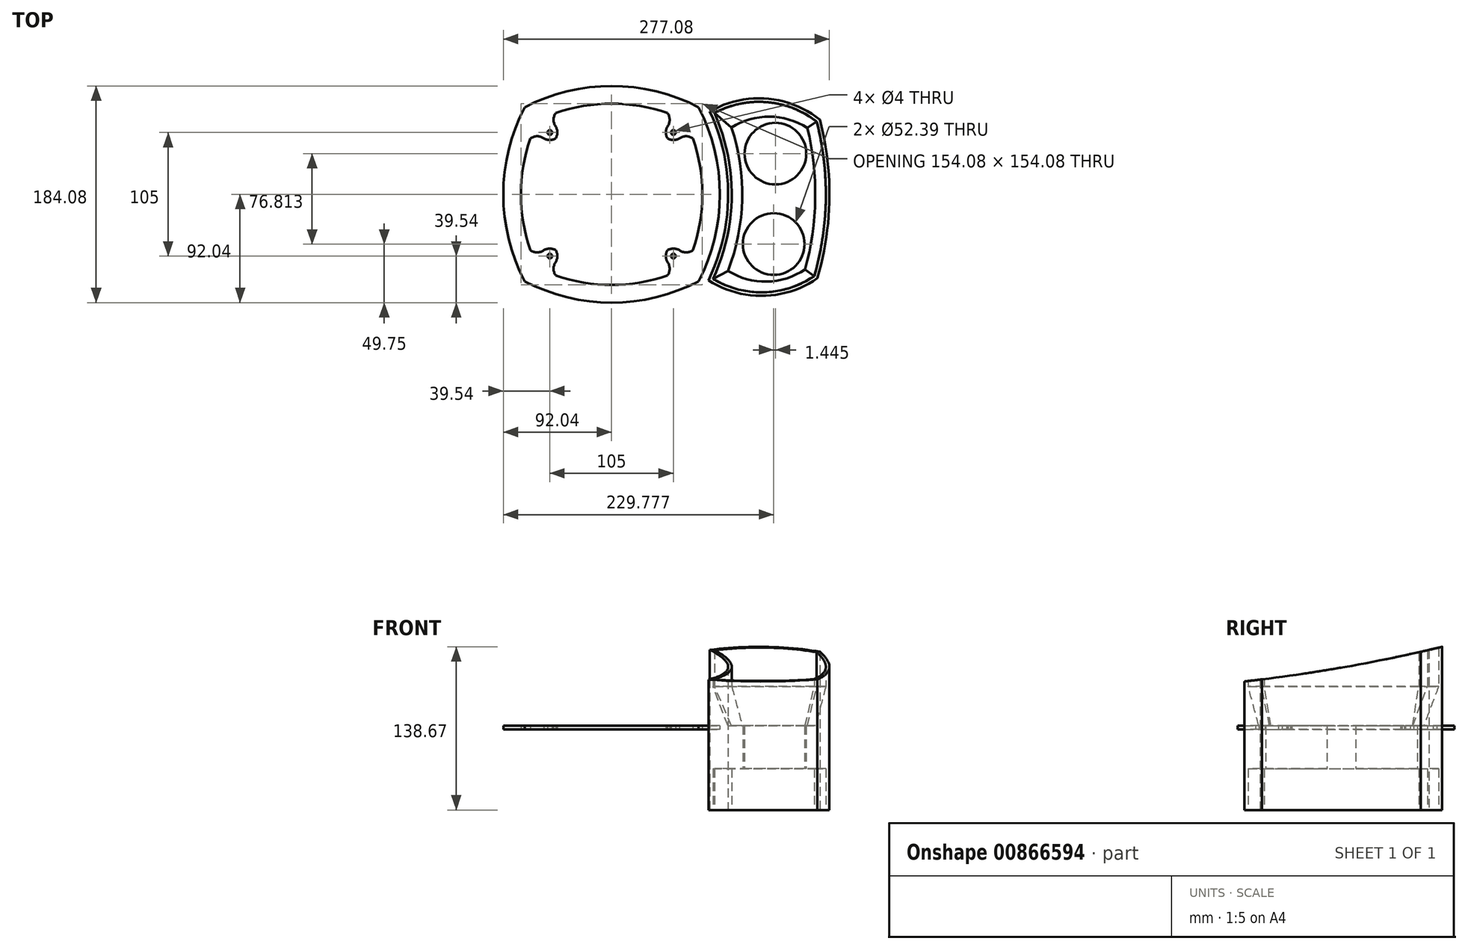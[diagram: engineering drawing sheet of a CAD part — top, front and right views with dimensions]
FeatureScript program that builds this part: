
annotation { "Feature Type Name" : "Feature", "Feature Type Description" : "" }
export const myFeature = defineFeature(function(context is Context, id is Id, definition is map)
    precondition{}
    {
        {
            var Q0;
            Q0=qCreatedBy(makeId("Top.planeOp"),FACE);
            var sketch = newSketch(context, id + "F0", { "sketchPlane" : qUnion([Q0])});
            skLineSegment(sketch, "E0.bottom", {"start": v(59, 59) * mm, "end": v(-59, 59) * mm, "construction": true});
            skLineSegment(sketch, "E0.top", {"start": v(59, -59) * mm, "end": v(-59, -59) * mm, "construction": true});
            skLineSegment(sketch, "E0.left", {"start": v(59, 59) * mm, "end": v(59, -59) * mm, "construction": true});
            skLineSegment(sketch, "E0.right", {"start": v(-59, 59) * mm, "end": v(-59, -59) * mm, "construction": true});
            skPoint(sketch, "E0.middle", {"position": v(0, 0) * mm});
            skArc(sketch, "E1", {"start": v(59, 59) * mm, "mid": v(0, 72.04) * mm, "end": v(-59, 59) * mm, "construction": true});
            skArc(sketch, "E2", {"start": v(59, -59) * mm, "mid": v(72.04, 0) * mm, "end": v(59, 59) * mm, "construction": true});
            skArc(sketch, "E3", {"start": v(-59, -59) * mm, "mid": v(0, -72.04) * mm, "end": v(59, -59) * mm, "construction": true});
            skArc(sketch, "E4", {"start": v(-59, 59) * mm, "mid": v(-72.04, 0) * mm, "end": v(-59, -59) * mm, "construction": true});
            skArc(sketch, "E5.0", {"start": v(62.76, 62.76) * mm, "mid": v(0, 77.04) * mm, "end": v(-62.76, 62.76) * mm});
            skArc(sketch, "E5.1", {"start": v(62.76, -62.76) * mm, "mid": v(77.04, 0) * mm, "end": v(62.76, 62.76) * mm});
            skArc(sketch, "E5.2", {"start": v(-62.76, -62.76) * mm, "mid": v(0, -77.04) * mm, "end": v(62.76, -62.76) * mm});
            skArc(sketch, "E5.3", {"start": v(-62.76, 62.76) * mm, "mid": v(-77.04, 0) * mm, "end": v(-62.76, -62.76) * mm});
            skArc(sketch, "E6.0", {"start": v(73.93, 73.93) * mm, "mid": v(0, 92.04) * mm, "end": v(-73.93, 73.93) * mm});
            skArc(sketch, "E6.1", {"start": v(73.93, -73.93) * mm, "mid": v(92.04, 0) * mm, "end": v(73.93, 73.93) * mm});
            skArc(sketch, "E6.2", {"start": v(-73.93, -73.93) * mm, "mid": v(0, -92.04) * mm, "end": v(73.93, -73.93) * mm});
            skArc(sketch, "E6.3", {"start": v(-73.93, 73.93) * mm, "mid": v(-92.04, 0) * mm, "end": v(-73.93, -73.93) * mm});
            skLineSegment(sketch, "E7.bottom", {"start": v(52.5, 52.5) * mm, "end": v(-52.5, 52.5) * mm, "construction": true});
            skLineSegment(sketch, "E7.top", {"start": v(52.5, -52.5) * mm, "end": v(-52.5, -52.5) * mm, "construction": true});
            skLineSegment(sketch, "E7.left", {"start": v(52.5, 52.5) * mm, "end": v(52.5, -52.5) * mm, "construction": true});
            skLineSegment(sketch, "E7.right", {"start": v(-52.5, 52.5) * mm, "end": v(-52.5, -52.5) * mm, "construction": true});
            skCircle(sketch, "E8", {"center": v(-52.5, 52.5) * mm, "radius": 2 * mm});
            skCircle(sketch, "E9", {"center": v(52.5, 52.5) * mm, "radius": 2 * mm});
            skCircle(sketch, "E10", {"center": v(52.5, -52.5) * mm, "radius": 2 * mm});
            skCircle(sketch, "E11", {"center": v(-52.5, -52.5) * mm, "radius": 2 * mm});
            skLineSegment(sketch, "E12.bottom", {"start": v(-47.5, 57.5) * mm, "end": v(-57.5, 57.5) * mm, "construction": true});
            skLineSegment(sketch, "E12.top", {"start": v(-47.5, 47.5) * mm, "end": v(-57.5, 47.5) * mm, "construction": true});
            skLineSegment(sketch, "E12.left", {"start": v(-47.5, 57.5) * mm, "end": v(-47.5, 47.5) * mm, "construction": true});
            skLineSegment(sketch, "E12.right", {"start": v(-57.5, 57.5) * mm, "end": v(-57.5, 47.5) * mm, "construction": true});
            skLineSegment(sketch, "E13.bottom", {"start": v(47.5, 57.5) * mm, "end": v(57.5, 57.5) * mm, "construction": true});
            skLineSegment(sketch, "E13.top", {"start": v(47.5, 47.5) * mm, "end": v(57.5, 47.5) * mm, "construction": true});
            skLineSegment(sketch, "E13.left", {"start": v(47.5, 57.5) * mm, "end": v(47.5, 47.5) * mm, "construction": true});
            skLineSegment(sketch, "E13.right", {"start": v(57.5, 57.5) * mm, "end": v(57.5, 47.5) * mm, "construction": true});
            skLineSegment(sketch, "E14.bottom", {"start": v(57.5, -47.5) * mm, "end": v(47.5, -47.5) * mm, "construction": true});
            skLineSegment(sketch, "E14.top", {"start": v(57.5, -57.5) * mm, "end": v(47.5, -57.5) * mm, "construction": true});
            skLineSegment(sketch, "E14.left", {"start": v(57.5, -47.5) * mm, "end": v(57.5, -57.5) * mm, "construction": true});
            skLineSegment(sketch, "E14.right", {"start": v(47.5, -47.5) * mm, "end": v(47.5, -57.5) * mm, "construction": true});
            skLineSegment(sketch, "E15.bottom", {"start": v(-47.5, -47.5) * mm, "end": v(-57.5, -47.5) * mm, "construction": true});
            skLineSegment(sketch, "E15.top", {"start": v(-47.5, -57.5) * mm, "end": v(-57.5, -57.5) * mm, "construction": true});
            skLineSegment(sketch, "E15.left", {"start": v(-47.5, -47.5) * mm, "end": v(-47.5, -57.5) * mm, "construction": true});
            skLineSegment(sketch, "E15.right", {"start": v(-57.5, -47.5) * mm, "end": v(-57.5, -57.5) * mm, "construction": true});
            skArc(sketch, "E16", {"start": v(-47.5, 57.5) * mm, "mid": v(-52.5, 58.84) * mm, "end": v(-57.5, 57.5) * mm});
            skArc(sketch, "E17", {"start": v(-47.5, 47.5) * mm, "mid": v(-46.16, 52.5) * mm, "end": v(-47.5, 57.5) * mm});
            skArc(sketch, "E18", {"start": v(-57.5, 47.5) * mm, "mid": v(-52.5, 46.16) * mm, "end": v(-47.5, 47.5) * mm});
            skArc(sketch, "E19", {"start": v(-57.5, 57.5) * mm, "mid": v(-58.84, 52.5) * mm, "end": v(-57.5, 47.5) * mm});
            skArc(sketch, "E20", {"start": v(-47.5, 69.04) * mm, "mid": v(-49.33, 63.27) * mm, "end": v(-47.5, 57.5) * mm});
            skArc(sketch, "E21", {"start": v(-57.5, 47.5) * mm, "mid": v(-63.27, 49.33) * mm, "end": v(-69.04, 47.5) * mm});
            skArc(sketch, "E22", {"start": v(47.5, 47.5) * mm, "mid": v(52.5, 46.16) * mm, "end": v(57.5, 47.5) * mm});
            skArc(sketch, "E23", {"start": v(47.5, 57.5) * mm, "mid": v(46.16, 52.5) * mm, "end": v(47.5, 47.5) * mm});
            skArc(sketch, "E24", {"start": v(57.5, 57.5) * mm, "mid": v(52.5, 58.84) * mm, "end": v(47.5, 57.5) * mm});
            skArc(sketch, "E25", {"start": v(57.5, 47.5) * mm, "mid": v(58.84, 52.5) * mm, "end": v(57.5, 57.5) * mm});
            skArc(sketch, "E26", {"start": v(47.5, 57.5) * mm, "mid": v(49.33, 63.27) * mm, "end": v(47.5, 69.04) * mm});
            skArc(sketch, "E27", {"start": v(69.04, 47.5) * mm, "mid": v(63.27, 49.33) * mm, "end": v(57.5, 47.5) * mm});
            skArc(sketch, "E28", {"start": v(57.5, -47.5) * mm, "mid": v(52.5, -46.16) * mm, "end": v(47.5, -47.5) * mm});
            skArc(sketch, "E29", {"start": v(47.5, -47.5) * mm, "mid": v(46.16, -52.5) * mm, "end": v(47.5, -57.5) * mm});
            skArc(sketch, "E30", {"start": v(47.5, -57.5) * mm, "mid": v(52.5, -58.84) * mm, "end": v(57.5, -57.5) * mm});
            skArc(sketch, "E31", {"start": v(57.5, -57.5) * mm, "mid": v(58.84, -52.5) * mm, "end": v(57.5, -47.5) * mm});
            skArc(sketch, "E32", {"start": v(57.5, -47.5) * mm, "mid": v(63.27, -49.33) * mm, "end": v(69.04, -47.5) * mm});
            skArc(sketch, "E33", {"start": v(47.5, -69.04) * mm, "mid": v(49.33, -63.27) * mm, "end": v(47.5, -57.5) * mm});
            skArc(sketch, "E34", {"start": v(-47.5, -47.5) * mm, "mid": v(-52.5, -46.16) * mm, "end": v(-57.5, -47.5) * mm});
            skArc(sketch, "E35", {"start": v(-47.5, -57.5) * mm, "mid": v(-46.16, -52.5) * mm, "end": v(-47.5, -47.5) * mm});
            skArc(sketch, "E36", {"start": v(-57.5, -57.5) * mm, "mid": v(-52.5, -58.84) * mm, "end": v(-47.5, -57.5) * mm});
            skArc(sketch, "E37", {"start": v(-57.5, -47.5) * mm, "mid": v(-58.84, -52.5) * mm, "end": v(-57.5, -57.5) * mm});
            skArc(sketch, "E38", {"start": v(-69.04, -47.5) * mm, "mid": v(-63.27, -49.33) * mm, "end": v(-57.5, -47.5) * mm});
            skArc(sketch, "E39", {"start": v(-47.5, -57.5) * mm, "mid": v(-49.33, -63.27) * mm, "end": v(-47.5, -69.04) * mm});
            skSolve(sketch);
        }
        {
            var Q0;
            Q0=makeQuery(id+"F0.imprint","IMPRINT",FACE,{"disambiguationData":[TD([[makeQuery(id+"F0.imprint","IMPRINT",EDGE,{"derivedFrom":sQuery(id+"F0.wireOp",EDGE,"E6.0")}),1.0]])]});
            var Q1;
            Q1=makeQuery(id+"F0.imprint","IMPRINT",FACE,{"disambiguationData":[TD([[makeQuery(id+"F0.imprint","IMPRINT",EDGE,{"derivedFrom":sQuery(id+"F0.wireOp",EDGE,"E16")}),-1.0]])]});
            var Q2;
            Q2=makeQuery(id+"F0.imprint","IMPRINT",FACE,{"disambiguationData":[TD([[makeQuery(id+"F0.imprint","IMPRINT",EDGE,{"derivedFrom":sQuery(id+"F0.wireOp",EDGE,"E8")}),-1.0]])]});
            var Q3;
            Q3=makeQuery(id+"F0.imprint","IMPRINT",FACE,{"disambiguationData":[TD([[makeQuery(id+"F0.imprint","IMPRINT",EDGE,{"derivedFrom":sQuery(id+"F0.wireOp",EDGE,"E24")}),-1.0]])]});
            var Q4;
            Q4=makeQuery(id+"F0.imprint","IMPRINT",FACE,{"disambiguationData":[TD([[makeQuery(id+"F0.imprint","IMPRINT",EDGE,{"derivedFrom":sQuery(id+"F0.wireOp",EDGE,"E9")}),-1.0]])]});
            var Q5;
            Q5=makeQuery(id+"F0.imprint","IMPRINT",FACE,{"disambiguationData":[TD([[makeQuery(id+"F0.imprint","IMPRINT",EDGE,{"derivedFrom":sQuery(id+"F0.wireOp",EDGE,"E30")}),-1.0]])]});
            var Q6;
            Q6=makeQuery(id+"F0.imprint","IMPRINT",FACE,{"disambiguationData":[TD([[makeQuery(id+"F0.imprint","IMPRINT",EDGE,{"derivedFrom":sQuery(id+"F0.wireOp",EDGE,"E10")}),-1.0]])]});
            var Q7;
            Q7=makeQuery(id+"F0.imprint","IMPRINT",FACE,{"disambiguationData":[TD([[makeQuery(id+"F0.imprint","IMPRINT",EDGE,{"derivedFrom":sQuery(id+"F0.wireOp",EDGE,"E36")}),-1.0]])]});
            var Q8;
            Q8=makeQuery(id+"F0.imprint","IMPRINT",FACE,{"disambiguationData":[TD([[makeQuery(id+"F0.imprint","IMPRINT",EDGE,{"derivedFrom":sQuery(id+"F0.wireOp",EDGE,"E11")}),-1.0]])]});
            extrude(context, id + "F1", {"entities" : qUnion([Q0, Q1, Q2, Q3, Q4, Q5, Q6, Q7, Q8]), "endBound" : BoundingType.SYMMETRIC, "depth" : 3 * mm, "offsetDistance" : 25 * mm});
        }
        {
            var Q0;
            Q0=qCreatedBy(makeId("Top.planeOp"),FACE);
            var sketch = newSketch(context, id + "F2", { "sketchPlane" : qUnion([Q0])});
            skCircle(sketch, "E40", {"center": v(139.18, 34.52) * mm, "radius": 26.2 * mm});
            skCircle(sketch, "E41.0", {"center": v(139.18, 34.52) * mm, "radius": 31.2 * mm});
            skCircle(sketch, "E42", {"center": v(137.74, -42.3) * mm, "radius": 26.2 * mm});
            skCircle(sketch, "E43.0", {"center": v(137.74, -42.3) * mm, "radius": 31.2 * mm});
            skArc(sketch, "E44.0", {"start": v(118.28, -97.04) * mm, "mid": v(142.04, 0) * mm, "end": v(118.28, 97.04) * mm, "construction": true});
            skArc(sketch, "E45.0", {"start": v(86.1, -71.87) * mm, "mid": v(102.03, -1.53) * mm, "end": v(87.37, 69.09) * mm});
            skArc(sketch, "E46.0", {"start": v(172.19, -69.5) * mm, "mid": v(182, -4.02) * mm, "end": v(174.3, 61.74) * mm});
            skArc(sketch, "E47", {"start": v(174.3, 61.74) * mm, "mid": v(131.92, 78.3) * mm, "end": v(87.37, 69.09) * mm});
            skArc(sketch, "E48", {"start": v(86.1, -71.87) * mm, "mid": v(129.5, -83.25) * mm, "end": v(172.19, -69.5) * mm});
            skArc(sketch, "E49.0", {"start": v(176.95, 63.47) * mm, "mid": v(131.29, 81.36) * mm, "end": v(83.5, 70.36) * mm});
            skArc(sketch, "E49.1", {"start": v(174.77, -71.36) * mm, "mid": v(185, -4.1) * mm, "end": v(176.95, 63.47) * mm});
            skArc(sketch, "E49.2", {"start": v(82.24, -73) * mm, "mid": v(128.75, -86.27) * mm, "end": v(174.77, -71.36) * mm});
            skArc(sketch, "E49.3", {"start": v(82.24, -73) * mm, "mid": v(99.03, -1.46) * mm, "end": v(83.5, 70.36) * mm});
            skSolve(sketch);
        }
        {
            var Q0;
            Q0=makeQuery(id+"F2.imprint","IMPRINT",FACE,{"disambiguationData":[TD([[makeQuery(id+"F2.imprint","IMPRINT",EDGE,{"derivedFrom":sQuery(id+"F2.wireOp",EDGE,"E45.0")}),1.0]])]});
            extrude(context, id + "F3", {"entities" : qUnion([Q0]), "endBound" : BoundingType.SYMMETRIC, "depth" : 140 * mm, "offsetDistance" : 25 * mm});
        }
        {
            var Q0;
            Q0=qCreatedBy(makeId("Right.planeOp"),FACE);
            var sketch = newSketch(context, id + "F4", { "sketchPlane" : qUnion([Q0])});
            skLineSegment(sketch, "E50", {"start": v(0, 0) * mm, "end": v(-487.6, 0) * mm, "construction": true});
            skCircle(sketch, "E51", {"center": v(-240, 1410) * mm, "radius": 1379.34 * mm});
            skCircle(sketch, "E52.MirrorC", {"center": v(-240, -1410) * mm, "radius": 1379.34 * mm});
            skSolve(sketch);
        }
        {
            var Q0;
            Q0=makeQuery(id+"F4.imprint","IMPRINT",FACE,{"disambiguationData":[TD([[makeQuery(id+"F4.imprint","IMPRINT",EDGE,{"derivedFrom":sQuery(id+"F4.wireOp",EDGE,"E51")}),1.0]])]});
            var Q1;
            Q1=makeQuery(id+"F4.imprint","IMPRINT",FACE,{"disambiguationData":[TD([[makeQuery(id+"F4.imprint","IMPRINT",EDGE,{"derivedFrom":sQuery(id+"F4.wireOp",EDGE,"E52.MirrorC")}),-1.0]])]});
            extrude(context, id + "F5", {"entities" : qUnion([Q0, Q1]), "operationType" : NewBodyOperationType.REMOVE, "depth" : 1210 * mm, "offsetDistance" : 25 * mm});
        }
        {
            var Q0;
            Q0=makeQuery(id+"F2.imprint","IMPRINT",FACE,{"disambiguationData":[TD([[makeQuery(id+"F2.imprint","IMPRINT",EDGE,{"derivedFrom":sQuery(id+"F2.wireOp",EDGE,"E41.0")}),-1.0]])]});
            var Q1;
            Q1=makeQuery(id+"F2.imprint","IMPRINT",FACE,{"disambiguationData":[TD([[makeQuery(id+"F2.imprint","IMPRINT",EDGE,{"derivedFrom":sQuery(id+"F2.wireOp",EDGE,"E40")}),-1.0]])]});
            var Q2;
            Q2=makeQuery(id+"F2.imprint","IMPRINT",FACE,{"disambiguationData":[TD([[makeQuery(id+"F2.imprint","IMPRINT",EDGE,{"derivedFrom":sQuery(id+"F2.wireOp",EDGE,"E42")}),-1.0]])]});
            extrude(context, id + "F6", {"entities" : qUnion([Q0, Q1, Q2]), "operationType" : NewBodyOperationType.ADD, "endBound" : BoundingType.SYMMETRIC, "depth" : 70 * mm, "offsetDistance" : 25 * mm});
        }
        {
            var Q0;
            Q0=makeQuery(id+"F6.opExtrude","CAP_FACE",FACE,{"disambiguationData":[OSD([sQuery(id+"F2.wireOp",EDGE,"E40"),sQuery(id+"F2.wireOp",EDGE,"E42"),sQuery(id+"F2.wireOp",EDGE,"E45.0"),sQuery(id+"F2.wireOp",EDGE,"E46.0"),sQuery(id+"F2.wireOp",EDGE,"E47"),sQuery(id+"F2.wireOp",EDGE,"E48")])],"isStart":false});
            var sketch = newSketch(context, id + "F7", { "sketchPlane" : qUnion([Q0])});
            skArc(sketch, "E53", {"start": v(174.3, 61.74) * mm, "mid": v(131.92, 78.3) * mm, "end": v(87.37, 69.09) * mm});
            skArc(sketch, "E54", {"start": v(172.19, -69.5) * mm, "mid": v(182, -4.02) * mm, "end": v(174.3, 61.74) * mm});
            skArc(sketch, "E55", {"start": v(86.1, -71.87) * mm, "mid": v(129.5, -83.25) * mm, "end": v(172.19, -69.5) * mm});
            skArc(sketch, "E56", {"start": v(86.1, -71.87) * mm, "mid": v(102.03, -1.53) * mm, "end": v(87.37, 69.09) * mm});
            skSolve(sketch);
        }
        {
            var Q0;
            Q0=qCreatedBy(makeId("Top.planeOp"),FACE);
            cPlane(context, id + "F8", {"entities" : qUnion([Q0]), "cplaneType" : CPlaneType.OFFSET, "offset" : 1.5 * mm, "width" : 150 * mm, "height" : 150 * mm});
        }
        {
            var Q0;
            Q0=qCreatedBy(id+"F8.planeOp",FACE);
            var sketch = newSketch(context, id + "F9", { "sketchPlane" : qUnion([Q0])});
            skArc(sketch, "E57.1", {"start": v(164.45, -63.78) * mm, "mid": v(173, -3.79) * mm, "end": v(166.34, 56.45) * mm});
            skArc(sketch, "E58.0", {"start": v(98.8, -65.03) * mm, "mid": v(110.98, -4.45) * mm, "end": v(101.83, 56.67) * mm});
            skArc(sketch, "E59", {"start": v(166.34, 56.45) * mm, "mid": v(134.12, 65.96) * mm, "end": v(101.83, 56.67) * mm});
            skArc(sketch, "E60", {"start": v(98.8, -65.03) * mm, "mid": v(131.81, -74.18) * mm, "end": v(164.45, -63.78) * mm});
            skSolve(sketch);
        }
        {
            var Q1;
            Q1 = qSketchRegion(id + "F9", true);
            var Q2;
            Q2 = qSketchRegion(id + "F7", true);
            loft(context, id + "F10", {"operationType" : NewBodyOperationType.REMOVE, "sheetProfilesArray" : [{ "sheetProfileEntities" : qUnion([Q1]) }, { "sheetProfileEntities" : qUnion([Q2]) }]});
        }
    });
